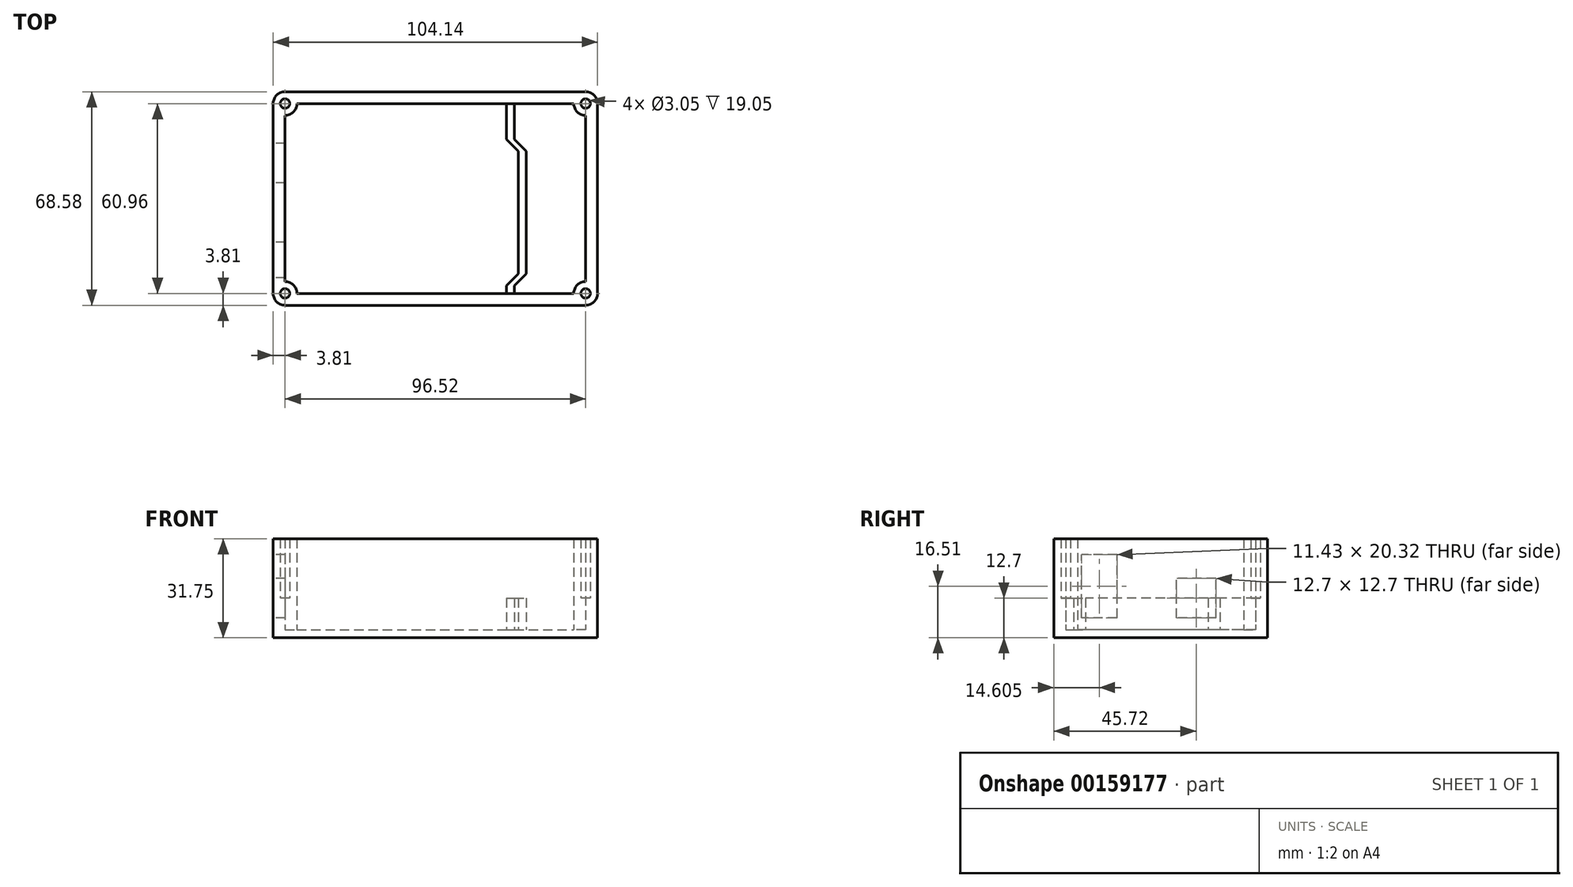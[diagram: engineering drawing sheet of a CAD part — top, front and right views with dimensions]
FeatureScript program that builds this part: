
annotation { "Feature Type Name" : "Feature", "Feature Type Description" : "" }
export const myFeature = defineFeature(function(context is Context, id is Id, definition is map)
    precondition{}
    {
        {
            var Q0;
            Q0=qCreatedBy(makeId("Top.planeOp"),FACE);
            var sketch = newSketch(context, id + "F0", { "sketchPlane" : qUnion([Q0])});
            skLineSegment(sketch, "E0.bottom", {"start": v(-52.07, 34.3) * mm, "end": v(52.07, 34.3) * mm});
            skLineSegment(sketch, "E0.top", {"start": v(-52.07, -34.3) * mm, "end": v(52.07, -34.3) * mm});
            skLineSegment(sketch, "E0.left", {"start": v(-52.07, 34.29) * mm, "end": v(-52.07, -34.29) * mm});
            skLineSegment(sketch, "E0.right", {"start": v(52.07, 34.29) * mm, "end": v(52.07, -34.29) * mm});
            skPoint(sketch, "E0.middle", {"position": v(0, 0) * mm});
            skLineSegment(sketch, "E1.bottom", {"start": v(-48.26, 30.48) * mm, "end": v(48.26, 30.48) * mm});
            skLineSegment(sketch, "E1.top", {"start": v(-48.26, -30.48) * mm, "end": v(48.26, -30.48) * mm});
            skLineSegment(sketch, "E1.left", {"start": v(-48.26, 30.48) * mm, "end": v(-48.26, -30.48) * mm});
            skLineSegment(sketch, "E1.right", {"start": v(48.26, 30.48) * mm, "end": v(48.26, -30.48) * mm});
            skLineSegment(sketch, "E2", {"start": v(-44.45, 34.29) * mm, "end": v(-44.45, -34.29) * mm, "construction": true});
            skLineSegment(sketch, "E3", {"start": v(44.45, 30.48) * mm, "end": v(44.45, -34.29) * mm, "construction": true});
            skLineSegment(sketch, "E4", {"start": v(-52.07, 26.67) * mm, "end": v(48.26, 26.67) * mm, "construction": true});
            skLineSegment(sketch, "E5", {"start": v(-52.07, -26.67) * mm, "end": v(52.07, -26.67) * mm, "construction": true});
            skLineSegment(sketch, "E6", {"start": v(-52.07, -34.29) * mm, "end": v(-44.45, -26.67) * mm, "construction": true});
            skCircle(sketch, "E7", {"center": v(-48.26, -30.48) * mm, "radius": 1.52 * mm});
            skLineSegment(sketch, "E8", {"start": v(-52.07, 34.29) * mm, "end": v(-44.45, 26.67) * mm, "construction": true});
            skCircle(sketch, "E9", {"center": v(-48.26, 30.48) * mm, "radius": 1.52 * mm});
            skLineSegment(sketch, "E10", {"start": v(44.45, 26.67) * mm, "end": v(52.07, 34.29) * mm, "construction": true});
            skCircle(sketch, "E11", {"center": v(48.26, 30.48) * mm, "radius": 1.52 * mm});
            skLineSegment(sketch, "E12", {"start": v(44.45, -26.67) * mm, "end": v(52.07, -34.3) * mm, "construction": true});
            skCircle(sketch, "E13", {"center": v(48.26, -30.48) * mm, "radius": 1.52 * mm});
            skLineSegment(sketch, "E14", {"start": v(22.86, 34.29) * mm, "end": v(22.86, -34.29) * mm, "construction": true});
            skLineSegment(sketch, "E15", {"start": v(25.4, 34.29) * mm, "end": v(25.4, -34.29) * mm, "construction": true});
            skLineSegment(sketch, "E16", {"start": v(26.67, 34.29) * mm, "end": v(26.67, -34.29) * mm, "construction": true});
            skLineSegment(sketch, "E17", {"start": v(29.21, 34.29) * mm, "end": v(29.21, -34.29) * mm, "construction": true});
            skLineSegment(sketch, "E18", {"start": v(3.05, 19.05) * mm, "end": v(24.22, 19.05) * mm, "construction": true});
            skLineSegment(sketch, "E19", {"start": v(4.38, -27.94) * mm, "end": v(25.4, -27.94) * mm, "construction": true});
            skLineSegment(sketch, "E20", {"start": v(22.86, -30.48) * mm, "end": v(22.86, -27.94) * mm});
            skLineSegment(sketch, "E21", {"start": v(25.4, -30.48) * mm, "end": v(25.4, -27.94) * mm});
            skLineSegment(sketch, "E22", {"start": v(25.4, -27.94) * mm, "end": v(29.21, -24.13) * mm});
            skLineSegment(sketch, "E23", {"start": v(22.86, -27.94) * mm, "end": v(26.67, -24.13) * mm});
            skLineSegment(sketch, "E24", {"start": v(22.86, 30.48) * mm, "end": v(22.86, 19.05) * mm});
            skLineSegment(sketch, "E25", {"start": v(25.4, 30.48) * mm, "end": v(25.4, 19.05) * mm});
            skLineSegment(sketch, "E26", {"start": v(25.4, 19.05) * mm, "end": v(29.21, 15.24) * mm});
            skLineSegment(sketch, "E27", {"start": v(22.86, 19.05) * mm, "end": v(26.67, 15.24) * mm});
            skLineSegment(sketch, "E28", {"start": v(26.67, 15.24) * mm, "end": v(26.67, -24.13) * mm});
            skLineSegment(sketch, "E29", {"start": v(29.21, 15.24) * mm, "end": v(29.21, -24.13) * mm});
            skLineSegment(sketch, "E30", {"start": v(-44.45, 30.48) * mm, "end": v(-44.45, 26.67) * mm});
            skLineSegment(sketch, "E31", {"start": v(-44.45, 26.67) * mm, "end": v(-48.26, 26.67) * mm});
            skLineSegment(sketch, "E32", {"start": v(-44.45, -30.48) * mm, "end": v(-44.45, -26.67) * mm});
            skLineSegment(sketch, "E33", {"start": v(-44.45, -26.67) * mm, "end": v(-48.26, -26.67) * mm});
            skLineSegment(sketch, "E34", {"start": v(44.45, -30.48) * mm, "end": v(44.45, -26.67) * mm});
            skLineSegment(sketch, "E35", {"start": v(44.45, -26.67) * mm, "end": v(48.26, -26.67) * mm});
            skLineSegment(sketch, "E36", {"start": v(44.45, 30.48) * mm, "end": v(44.45, 26.67) * mm});
            skLineSegment(sketch, "E37", {"start": v(44.45, 26.67) * mm, "end": v(48.26, 26.67) * mm});
            skSolve(sketch);
        }
        {
            var Q0;
            Q0=makeQuery(id+"F0.imprint","IMPRINT",FACE,{"disambiguationData":[TD([[makeQuery(id+"F0.imprint","IMPRINT",EDGE,{"derivedFrom":sQuery(id+"F0.wireOp",EDGE,"E0.bottom")}),-1.0]])]});
            var Q1;
            {var subQ0=sQuery(id+"F0.wireOp",EDGE,"E36");Q1=makeQuery(id+"F0.imprint","IMPRINT",FACE,{"disambiguationData":[TD([[makeQuery(id+"F0.imprint","IMPRINT",EDGE,{"derivedFrom":subQ0}),1.0]])]});}
            var Q2;
            {var subQ0=sQuery(id+"F0.wireOp",EDGE,"E34");Q2=makeQuery(id+"F0.imprint","IMPRINT",FACE,{"disambiguationData":[TD([[makeQuery(id+"F0.imprint","IMPRINT",EDGE,{"derivedFrom":subQ0}),-1.0]])]});}
            var Q3;
            {var subQ0=sQuery(id+"F0.wireOp",EDGE,"E32");Q3=makeQuery(id+"F0.imprint","IMPRINT",FACE,{"disambiguationData":[TD([[makeQuery(id+"F0.imprint","IMPRINT",EDGE,{"derivedFrom":subQ0}),1.0]])]});}
            var Q4;
            {var subQ0=sQuery(id+"F0.wireOp",EDGE,"E30");Q4=makeQuery(id+"F0.imprint","IMPRINT",FACE,{"disambiguationData":[TD([[makeQuery(id+"F0.imprint","IMPRINT",EDGE,{"derivedFrom":subQ0}),-1.0]])]});}
            extrude(context, id + "F1", {"entities" : qUnion([Q0, Q1, Q2, Q3, Q4]), "depth" : 31.75 * mm});
        }
        {
            var Q0;
            {var subQ2=sQuery(id+"F0.wireOp",EDGE,"E20");Q0=makeQuery(id+"F0.imprint","IMPRINT",FACE,{"disambiguationData":[TD([[makeQuery(id+"F0.imprint","IMPRINT",EDGE,{"derivedFrom":subQ2}),-1.0]])]});}
            extrude(context, id + "F2", {"entities" : qUnion([Q0]), "operationType" : NewBodyOperationType.ADD, "depth" : 12.7 * mm});
        }
        {
            var Q0;
            {var subQ7=sQuery(id+"F0.wireOp",EDGE,"E20");Q0=makeQuery(id+"F0.imprint","IMPRINT",FACE,{"disambiguationData":[TD([[makeQuery(id+"F0.imprint","IMPRINT",EDGE,{"derivedFrom":subQ7}),1.0]])]});}
            var Q1;
            {var subQ5=sQuery(id+"F0.wireOp",EDGE,"E21");Q1=makeQuery(id+"F0.imprint","IMPRINT",FACE,{"disambiguationData":[TD([[makeQuery(id+"F0.imprint","IMPRINT",EDGE,{"derivedFrom":subQ5}),-1.0]])]});}
            extrude(context, id + "F3", {"entities" : qUnion([Q0, Q1]), "operationType" : NewBodyOperationType.ADD, "depth" : 2.54 * mm});
        }
        {
            var Q0;
            Q0=makeQuery(id+"F1.opExtrude","SWEPT_FACE",FACE,{"disambiguationData":[OSD([sQuery(id+"F0.wireOp",EDGE,"E0.left")])]});
            var sketch = newSketch(context, id + "F4", { "sketchPlane" : qUnion([Q0])});
            skLineSegment(sketch, "E38.bottom", {"start": v(-17.78, 6.35) * mm, "end": v(-5.08, 6.35) * mm});
            skLineSegment(sketch, "E38.top", {"start": v(-17.78, 19.05) * mm, "end": v(-5.08, 19.05) * mm});
            skLineSegment(sketch, "E38.left", {"start": v(-17.78, 6.35) * mm, "end": v(-17.78, 19.05) * mm});
            skLineSegment(sketch, "E38.right", {"start": v(-5.08, 6.35) * mm, "end": v(-5.08, 19.05) * mm});
            skLineSegment(sketch, "E39.bottom", {"start": v(13.97, 6.35) * mm, "end": v(25.4, 6.35) * mm});
            skLineSegment(sketch, "E39.top", {"start": v(13.97, 26.67) * mm, "end": v(25.4, 26.67) * mm});
            skLineSegment(sketch, "E39.left", {"start": v(13.97, 6.35) * mm, "end": v(13.97, 26.67) * mm});
            skLineSegment(sketch, "E39.right", {"start": v(25.4, 6.35) * mm, "end": v(25.4, 26.67) * mm});
            skSolve(sketch);
        }
        {
            var Q0;
            Q0=makeQuery(id+"F4.imprint","IMPRINT",FACE,{"disambiguationData":[TD([[makeQuery(id+"F4.imprint","IMPRINT",EDGE,{"derivedFrom":sQuery(id+"F4.wireOp",EDGE,"E38.bottom")}),1.0]])]});
            var Q1;
            Q1=makeQuery(id+"F4.imprint","IMPRINT",FACE,{"disambiguationData":[TD([[makeQuery(id+"F4.imprint","IMPRINT",EDGE,{"derivedFrom":sQuery(id+"F4.wireOp",EDGE,"E39.bottom")}),1.0]])]});
            extrude(context, id + "F5", {"entities" : qUnion([Q0, Q1]), "operationType" : NewBodyOperationType.REMOVE, "oppositeDirection" : true, "depth" : 10.16 * mm});
        }
        {
            var Q0;
            Q0=makeQuery(id+"F1.opExtrude","SWEPT_EDGE",EDGE,{"disambiguationData":[OSD([sQuery(id+"F0.wireOp",EDGE,"E0.top"),sQuery(id+"F0.wireOp",EDGE,"E0.left")])]});
            var Q1;
            Q1=makeQuery(id+"F1.opExtrude","SWEPT_EDGE",EDGE,{"disambiguationData":[OSD([sQuery(id+"F0.wireOp",EDGE,"E0.top"),sQuery(id+"F0.wireOp",EDGE,"E0.right")])]});
            var Q2;
            Q2=makeQuery(id+"F1.opExtrude","SWEPT_EDGE",EDGE,{"disambiguationData":[OSD([sQuery(id+"F0.wireOp",EDGE,"E0.bottom"),sQuery(id+"F0.wireOp",EDGE,"E0.right")])]});
            var Q3;
            Q3=makeQuery(id+"F1.opExtrude","SWEPT_EDGE",EDGE,{"disambiguationData":[OSD([sQuery(id+"F0.wireOp",EDGE,"E0.bottom"),sQuery(id+"F0.wireOp",EDGE,"E0.left")])]});
            fillet(context, id + "F6", {"entities" : qUnion([Q0, Q1, Q2, Q3]), "radius" : 3.8 * mm, "tangentPropagation" : true, "allowEdgeOverflow" : false});
        }
        {
            var Q0;
            Q0=makeQuery(id+"F1.opExtrude","SWEPT_EDGE",EDGE,{"disambiguationData":[OSD([sQuery(id+"F0.wireOp",EDGE,"E36"),sQuery(id+"F0.wireOp",EDGE,"E37")])]});
            var Q1;
            Q1=makeQuery(id+"F1.opExtrude","SWEPT_EDGE",EDGE,{"disambiguationData":[OSD([sQuery(id+"F0.wireOp",EDGE,"E30"),sQuery(id+"F0.wireOp",EDGE,"E31")])]});
            var Q2;
            Q2=makeQuery(id+"F1.opExtrude","SWEPT_EDGE",EDGE,{"disambiguationData":[OSD([sQuery(id+"F0.wireOp",EDGE,"E34"),sQuery(id+"F0.wireOp",EDGE,"E35")])]});
            var Q3;
            Q3=makeQuery(id+"F1.opExtrude","SWEPT_EDGE",EDGE,{"disambiguationData":[OSD([sQuery(id+"F0.wireOp",EDGE,"E32"),sQuery(id+"F0.wireOp",EDGE,"E33")])]});
            fillet(context, id + "F7", {"entities" : qUnion([Q0, Q1, Q2, Q3]), "radius" : 3.8 * mm, "tangentPropagation" : true, "allowEdgeOverflow" : false});
        }
        {
            var Q0;
            {var subQ0=sQuery(id+"F0.wireOp",EDGE,"E1.left");var subQ1=sQuery(id+"F0.wireOp",EDGE,"E1.bottom");var subQ2=makeQuery(id+"F0.imprint","INTERSECT",VERTEX,{"derivedFrom":[subQ1,subQ0]});Q0=makeQuery(id+"F0.imprint","IMPRINT",FACE,{"disambiguationData":[TD([[makeQuery(id+"F0.imprint","IMPRINT",EDGE,{"disambiguationData":[TD([[subQ2,-1.0]])],"derivedFrom":subQ1}),1.0]])]});}
            var Q1;
            {var subQ0=sQuery(id+"F0.wireOp",EDGE,"E1.right");var subQ1=sQuery(id+"F0.wireOp",EDGE,"E1.bottom");var subQ2=makeQuery(id+"F0.imprint","INTERSECT",VERTEX,{"derivedFrom":[subQ1,subQ0]});Q1=makeQuery(id+"F0.imprint","IMPRINT",FACE,{"disambiguationData":[TD([[makeQuery(id+"F0.imprint","IMPRINT",EDGE,{"disambiguationData":[TD([[subQ2,1.0]])],"derivedFrom":subQ1}),-1.0]])]});}
            var Q2;
            {var subQ0=sQuery(id+"F0.wireOp",EDGE,"E1.right");var subQ1=sQuery(id+"F0.wireOp",EDGE,"E1.bottom");var subQ2=makeQuery(id+"F0.imprint","INTERSECT",VERTEX,{"derivedFrom":[subQ1,subQ0]});Q2=makeQuery(id+"F0.imprint","IMPRINT",FACE,{"disambiguationData":[TD([[makeQuery(id+"F0.imprint","IMPRINT",EDGE,{"disambiguationData":[TD([[subQ2,1.0]])],"derivedFrom":subQ1}),1.0]])]});}
            var Q3;
            {var subQ0=sQuery(id+"F0.wireOp",EDGE,"E1.left");var subQ1=sQuery(id+"F0.wireOp",EDGE,"E1.bottom");var subQ2=makeQuery(id+"F0.imprint","INTERSECT",VERTEX,{"derivedFrom":[subQ1,subQ0]});Q3=makeQuery(id+"F0.imprint","IMPRINT",FACE,{"disambiguationData":[TD([[makeQuery(id+"F0.imprint","IMPRINT",EDGE,{"disambiguationData":[TD([[subQ2,-1.0]])],"derivedFrom":subQ1}),-1.0]])]});}
            var Q4;
            {var subQ0=sQuery(id+"F0.wireOp",EDGE,"E1.left");var subQ1=sQuery(id+"F0.wireOp",EDGE,"E1.top");var subQ2=makeQuery(id+"F0.imprint","INTERSECT",VERTEX,{"derivedFrom":[subQ1,subQ0]});Q4=makeQuery(id+"F0.imprint","IMPRINT",FACE,{"disambiguationData":[TD([[makeQuery(id+"F0.imprint","IMPRINT",EDGE,{"disambiguationData":[TD([[subQ2,-1.0]])],"derivedFrom":subQ1}),-1.0]])]});}
            var Q5;
            {var subQ0=sQuery(id+"F0.wireOp",EDGE,"E1.left");var subQ1=sQuery(id+"F0.wireOp",EDGE,"E1.top");var subQ2=makeQuery(id+"F0.imprint","INTERSECT",VERTEX,{"derivedFrom":[subQ1,subQ0]});Q5=makeQuery(id+"F0.imprint","IMPRINT",FACE,{"disambiguationData":[TD([[makeQuery(id+"F0.imprint","IMPRINT",EDGE,{"disambiguationData":[TD([[subQ2,-1.0]])],"derivedFrom":subQ1}),1.0]])]});}
            var Q6;
            {var subQ0=sQuery(id+"F0.wireOp",EDGE,"E1.right");var subQ1=sQuery(id+"F0.wireOp",EDGE,"E1.top");var subQ2=makeQuery(id+"F0.imprint","INTERSECT",VERTEX,{"derivedFrom":[subQ1,subQ0]});Q6=makeQuery(id+"F0.imprint","IMPRINT",FACE,{"disambiguationData":[TD([[makeQuery(id+"F0.imprint","IMPRINT",EDGE,{"disambiguationData":[TD([[subQ2,1.0]])],"derivedFrom":subQ1}),-1.0]])]});}
            var Q7;
            {var subQ0=sQuery(id+"F0.wireOp",EDGE,"E1.right");var subQ1=sQuery(id+"F0.wireOp",EDGE,"E1.top");var subQ2=makeQuery(id+"F0.imprint","INTERSECT",VERTEX,{"derivedFrom":[subQ1,subQ0]});Q7=makeQuery(id+"F0.imprint","IMPRINT",FACE,{"disambiguationData":[TD([[makeQuery(id+"F0.imprint","IMPRINT",EDGE,{"disambiguationData":[TD([[subQ2,1.0]])],"derivedFrom":subQ1}),1.0]])]});}
            extrude(context, id + "F8", {"entities" : qUnion([Q0, Q1, Q2, Q3, Q4, Q5, Q6, Q7]), "operationType" : NewBodyOperationType.ADD, "depth" : 12.7 * mm});
        }
    });
